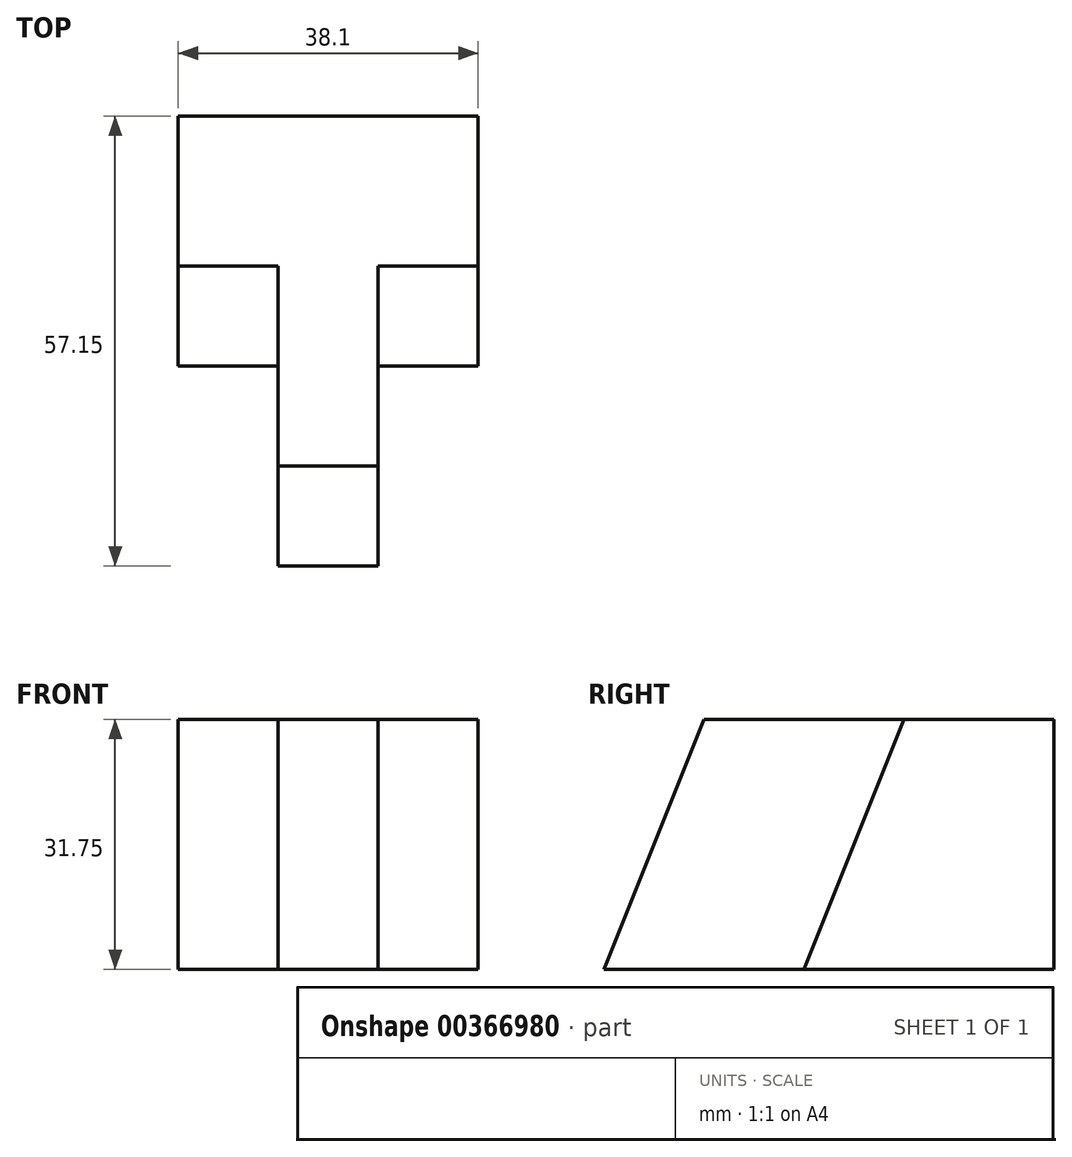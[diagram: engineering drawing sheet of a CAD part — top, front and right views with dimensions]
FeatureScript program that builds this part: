
annotation { "Feature Type Name" : "Feature", "Feature Type Description" : "" }
export const myFeature = defineFeature(function(context is Context, id is Id, definition is map)
    precondition{}
    {
        {
            var Q0;
            Q0=qCreatedBy(makeId("Top.planeOp"),FACE);
            var sketch = newSketch(context, id + "F0", { "sketchPlane" : qUnion([Q0])});
            skLineSegment(sketch, "E0", {"start": v(0, 0) * mm, "end": v(0, 31.75) * mm});
            skLineSegment(sketch, "E1", {"start": v(0, 31.75) * mm, "end": v(38.1, 31.75) * mm});
            skLineSegment(sketch, "E2", {"start": v(38.1, 31.75) * mm, "end": v(38.1, 0) * mm});
            skLineSegment(sketch, "E3", {"start": v(38.1, 0) * mm, "end": v(25.4, 0) * mm});
            skLineSegment(sketch, "E4", {"start": v(25.4, 0) * mm, "end": v(25.4, -25.4) * mm});
            skLineSegment(sketch, "E5", {"start": v(25.4, -25.4) * mm, "end": v(12.7, -25.4) * mm});
            skLineSegment(sketch, "E6", {"start": v(12.7, -25.4) * mm, "end": v(12.7, 0) * mm});
            skLineSegment(sketch, "E7", {"start": v(12.7, 0) * mm, "end": v(0, 0) * mm});
            skSolve(sketch);
        }
        {
            var Q0;
            Q0=makeQuery(id+"F0.imprint","IMPRINT",FACE,{"disambiguationData":[TD([[makeQuery(id+"F0.imprint","IMPRINT",EDGE,{"derivedFrom":sQuery(id+"F0.wireOp",EDGE,"E0")}),-1.0]])]});
            extrude(context, id + "F1", {"entities" : qUnion([Q0]), "depth" : 31.75 * mm});
        }
        {
            var Q0;
            Q0=makeQuery(id+"F1.opExtrude","SWEPT_FACE",FACE,{"disambiguationData":[OSD([sQuery(id+"F0.wireOp",EDGE,"E6")])]});
            var sketch = newSketch(context, id + "F2", { "sketchPlane" : qUnion([Q0])});
            skLineSegment(sketch, "E8", {"start": v(12.7, 31.75) * mm, "end": v(25.4, 0) * mm});
            skSolve(sketch);
        }
        {
            var Q0;
            {var subQ0=sQuery(id+"F2.wireOp",EDGE,"E8");Q0=makeQuery(id+"F2.imprint","IMPRINT",FACE,{"disambiguationData":[TD([[makeQuery(id+"F2.imprint","IMPRINT",EDGE,{"derivedFrom":subQ0}),1.0]])]});}
            extrude(context, id + "F3", {"entities" : qUnion([Q0]), "operationType" : NewBodyOperationType.REMOVE, "oppositeDirection" : true, "depth" : 12.7 * mm});
        }
        {
            var Q0;
            Q0=makeQuery(id+"F1.opExtrude","SWEPT_FACE",FACE,{"disambiguationData":[OSD([sQuery(id+"F0.wireOp",EDGE,"E0")])]});
            var sketch = newSketch(context, id + "F4", { "sketchPlane" : qUnion([Q0])});
            skLineSegment(sketch, "E9", {"start": v(-12.7, 31.75) * mm, "end": v(0, 0) * mm});
            skSolve(sketch);
        }
        {
            var Q0;
            {var subQ0=sQuery(id+"F4.wireOp",EDGE,"E9");Q0=makeQuery(id+"F4.imprint","IMPRINT",FACE,{"disambiguationData":[TD([[makeQuery(id+"F4.imprint","IMPRINT",EDGE,{"derivedFrom":subQ0}),1.0]])]});}
            extrude(context, id + "F5", {"entities" : qUnion([Q0]), "operationType" : NewBodyOperationType.REMOVE, "oppositeDirection" : true, "depth" : 12.7 * mm});
        }
        {
            var Q0;
            Q0=makeQuery(id+"F1.opExtrude","SWEPT_FACE",FACE,{"disambiguationData":[OSD([sQuery(id+"F0.wireOp",EDGE,"E2")])]});
            var sketch = newSketch(context, id + "F6", { "sketchPlane" : qUnion([Q0])});
            skLineSegment(sketch, "E10", {"start": v(0, 0) * mm, "end": v(12.7, 31.75) * mm});
            skSolve(sketch);
        }
        {
            var Q0;
            {var subQ0=sQuery(id+"F6.wireOp",EDGE,"E10");Q0=makeQuery(id+"F6.imprint","IMPRINT",FACE,{"disambiguationData":[TD([[makeQuery(id+"F6.imprint","IMPRINT",EDGE,{"derivedFrom":subQ0}),1.0]])]});}
            extrude(context, id + "F7", {"entities" : qUnion([Q0]), "operationType" : NewBodyOperationType.REMOVE, "oppositeDirection" : true, "depth" : 12.7 * mm});
        }
    });
